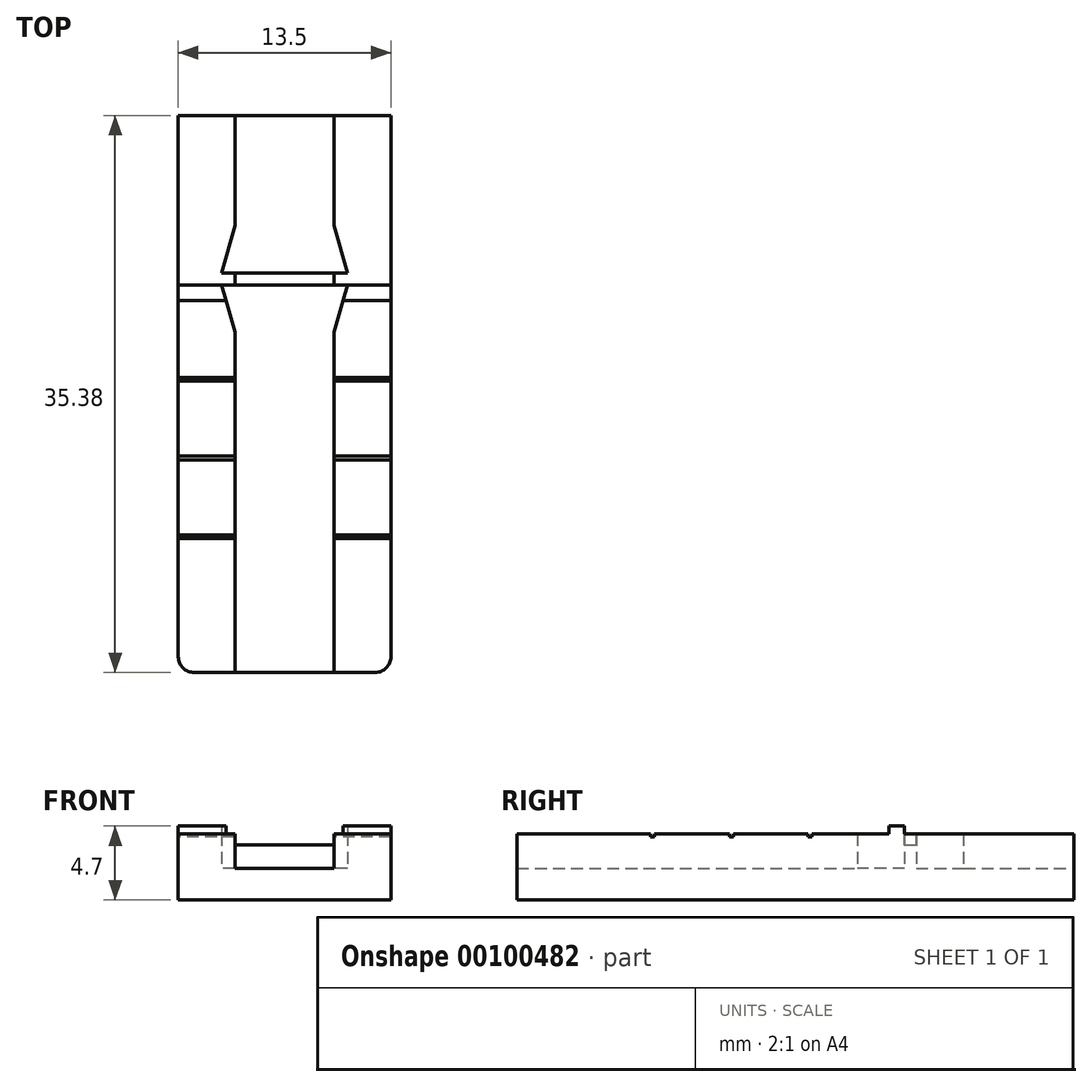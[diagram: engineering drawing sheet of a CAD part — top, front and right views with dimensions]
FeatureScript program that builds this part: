
annotation { "Feature Type Name" : "Feature", "Feature Type Description" : "" }
export const myFeature = defineFeature(function(context is Context, id is Id, definition is map)
    precondition{}
    {
        {
            var Q0;
            Q0=qCreatedBy(makeId("Front.planeOp"),FACE);
            var sketch = newSketch(context, id + "F0", { "sketchPlane" : qUnion([Q0])});
            skLineSegment(sketch, "E0", {"start": v(-6.75, 0) * mm, "end": v(6.75, 0) * mm});
            skLineSegment(sketch, "E1", {"start": v(6.75, 0) * mm, "end": v(6.75, 4.2) * mm});
            skLineSegment(sketch, "E2", {"start": v(6.75, 4.2) * mm, "end": v(3.15, 4.2) * mm});
            skLineSegment(sketch, "E3", {"start": v(3.15, 4.2) * mm, "end": v(3.15, 2) * mm});
            skLineSegment(sketch, "E4", {"start": v(3.15, 2) * mm, "end": v(-3.15, 2) * mm});
            skLineSegment(sketch, "E5", {"start": v(-3.15, 2) * mm, "end": v(-3.15, 4.2) * mm});
            skLineSegment(sketch, "E6", {"start": v(-3.15, 4.2) * mm, "end": v(-6.75, 4.2) * mm});
            skLineSegment(sketch, "E7", {"start": v(-6.75, 4.2) * mm, "end": v(-6.75, 0) * mm});
            skPoint(sketch, "E8", {"position": v(0, 2) * mm});
            skSolve(sketch);
        }
        {
            var Q0;
            Q0=qSketchRegion(id+"F0",true);
            extrude(context, id + "F1", {"entities" : qUnion([Q0]), "endBound" : BoundingType.SYMMETRIC, "depth" : 50 * mm});
        }
        {
            var Q0;
            Q0=makeQuery(id+"F1.opExtrude","SWEPT_FACE",FACE,{"disambiguationData":[OSD([sQuery(id+"F0.wireOp",EDGE,"E4")])]});
            var sketch = newSketch(context, id + "F2", { "sketchPlane" : qUnion([Q0])});
            skLineSegment(sketch, "E9.bottom", {"start": v(3.15, 0.38) * mm, "end": v(-3.15, 0.38) * mm});
            skLineSegment(sketch, "E9.top", {"start": v(3.15, -0.38) * mm, "end": v(-3.15, -0.38) * mm});
            skLineSegment(sketch, "E9.left", {"start": v(3.15, 0.38) * mm, "end": v(3.15, -0.38) * mm});
            skLineSegment(sketch, "E9.right", {"start": v(-3.15, 0.38) * mm, "end": v(-3.15, -0.38) * mm});
            skPoint(sketch, "E9.middle", {"position": v(0, 0) * mm});
            skSolve(sketch);
        }
        {
            var Q0;
            Q0=qSketchRegion(id+"F2",true);
            extrude(context, id + "F3", {"entities" : qUnion([Q0]), "operationType" : NewBodyOperationType.ADD, "depth" : 1.5 * mm});
        }
        {
            var Q0;
            Q0=makeQuery(id+"F1.opExtrude","SWEPT_FACE",FACE,{"disambiguationData":[OSD([sQuery(id+"F0.wireOp",EDGE,"E6")])]});
            var sketch = newSketch(context, id + "F4", { "sketchPlane" : qUnion([Q0])});
            skLineSegment(sketch, "E10.bottom", {"start": v(6.75, -0.37) * mm, "end": v(-6.75, -0.38) * mm});
            skLineSegment(sketch, "E10.top", {"start": v(6.75, -1.37) * mm, "end": v(-6.75, -1.38) * mm});
            skLineSegment(sketch, "E10.left", {"start": v(6.75, -0.38) * mm, "end": v(6.75, -1.37) * mm});
            skLineSegment(sketch, "E10.right", {"start": v(-6.75, -0.38) * mm, "end": v(-6.75, -1.38) * mm});
            skLineSegment(sketch, "E11", {"start": v(-3.15, -0.38) * mm, "end": v(-3.15, -1.38) * mm});
            skLineSegment(sketch, "E12", {"start": v(3.15, -1.38) * mm, "end": v(3.15, -0.38) * mm});
            skSolve(sketch);
        }
        {
            var Q0;
            {var subQ0=sQuery(id+"F4.wireOp",EDGE,"E10.left");Q0=makeQuery(id+"F4.imprint","IMPRINT",FACE,{"disambiguationData":[TD([[makeQuery(id+"F4.imprint","IMPRINT",EDGE,{"derivedFrom":subQ0}),-1.0]])]});}
            var Q1;
            {var subQ0=sQuery(id+"F4.wireOp",EDGE,"E10.right");Q1=makeQuery(id+"F4.imprint","IMPRINT",FACE,{"disambiguationData":[TD([[makeQuery(id+"F4.imprint","IMPRINT",EDGE,{"derivedFrom":subQ0}),-1.0]])]});}
            extrude(context, id + "F5", {"entities" : qUnion([Q0, Q1]), "operationType" : NewBodyOperationType.ADD, "depth" : .5 * mm});
        }
        {
            var Q0;
            {var subQ1=sQuery(id+"F4.wireOp",EDGE,"E10.right");var subQ2=sQuery(id+"F4.wireOp",EDGE,"E10.top");var subQ3=sQuery(id+"F0.wireOp",EDGE,"E7");var subQ4=sQuery(id+"F0.wireOp",EDGE,"E6");Q0=makeQuery(id+"F5.boolean.opBoolean","SPLIT",FACE,{"disambiguationData":[TD([makeQuery(id+"F5.opExtrude","SWEPT_FACE",FACE,{"disambiguationData":[OSD([subQ2]),TDD([makeQuery(id+"F4.imprint","IMPRINT",EDGE,{"disambiguationData":[TD([[makeQuery(id+"F4.imprint","INTERSECT",VERTEX,{"derivedFrom":[makeQuery(id+"F1.opExtrude","SWEPT_EDGE",EDGE,{"disambiguationData":[OSD([subQ4,subQ3])]}),subQ2,subQ1]}),1.0]])],"derivedFrom":subQ2})])]})])],"derivedFrom":makeQuery(id+"F1.opExtrude","SWEPT_FACE",FACE,{"disambiguationData":[OSD([subQ4])]})});}
            var sketch = newSketch(context, id + "F6", { "sketchPlane" : qUnion([Q0])});
            skLineSegment(sketch, "E13.bottom", {"start": v(6.75, -6.5) * mm, "end": v(-6.75, -6.5) * mm});
            skLineSegment(sketch, "E13.top", {"start": v(6.75, -6.25) * mm, "end": v(-6.75, -6.25) * mm});
            skLineSegment(sketch, "E13.left", {"start": v(6.75, -6.5) * mm, "end": v(6.75, -6.25) * mm});
            skLineSegment(sketch, "E13.right", {"start": v(-6.75, -6.5) * mm, "end": v(-6.75, -6.25) * mm});
            skPoint(sketch, "E13.middle", {"position": v(0, -6.37) * mm});
            skLineSegment(sketch, "E14.bottom", {"start": v(6.75, -11.5) * mm, "end": v(-6.75, -11.5) * mm});
            skLineSegment(sketch, "E14.top", {"start": v(6.75, -11.25) * mm, "end": v(-6.75, -11.25) * mm});
            skLineSegment(sketch, "E14.left", {"start": v(6.75, -11.5) * mm, "end": v(6.75, -11.25) * mm});
            skLineSegment(sketch, "E14.right", {"start": v(-6.75, -11.5) * mm, "end": v(-6.75, -11.25) * mm});
            skPoint(sketch, "E14.middle", {"position": v(0, -11.37) * mm});
            skLineSegment(sketch, "E15.bottom", {"start": v(6.75, -16.5) * mm, "end": v(-6.75, -16.5) * mm});
            skLineSegment(sketch, "E15.top", {"start": v(6.75, -16.25) * mm, "end": v(-6.75, -16.25) * mm});
            skLineSegment(sketch, "E15.left", {"start": v(6.75, -16.5) * mm, "end": v(6.75, -16.25) * mm});
            skLineSegment(sketch, "E15.right", {"start": v(-6.75, -16.5) * mm, "end": v(-6.75, -16.25) * mm});
            skPoint(sketch, "E15.middle", {"position": v(0, -16.37) * mm});
            skSolve(sketch);
        }
        {
            var Q0;
            Q0=qSketchRegion(id+"F6",true);
            extrude(context, id + "F7", {"entities" : qUnion([Q0]), "operationType" : NewBodyOperationType.REMOVE, "oppositeDirection" : true, "depth" : .2 * mm});
        }
        {
            var Q0;
            {var subQ0=sQuery(id+"F4.wireOp",EDGE,"E10.left");var subQ1=sQuery(id+"F4.wireOp",EDGE,"E10.bottom");var subQ5=sQuery(id+"F0.wireOp",EDGE,"E2");Q0=makeQuery(id+"F5.boolean.opBoolean","SPLIT",FACE,{"disambiguationData":[TD([makeQuery(id+"F5.opExtrude","SWEPT_FACE",FACE,{"disambiguationData":[OSD([subQ1]),TDD([makeQuery(id+"F4.imprint","IMPRINT",EDGE,{"disambiguationData":[TD([[makeQuery(id+"F4.imprint","INTERSECT",VERTEX,{"derivedFrom":[subQ1,subQ0]}),-1.0]])],"derivedFrom":subQ1})])]})])],"derivedFrom":makeQuery(id+"F1.opExtrude","SWEPT_FACE",FACE,{"disambiguationData":[OSD([subQ5])]})});}
            var sketch = newSketch(context, id + "F8", { "sketchPlane" : qUnion([Q0])});
            skLineSegment(sketch, "E16.bottom", {"start": v(6.75, 25) * mm, "end": v(-6.75, 25) * mm});
            skLineSegment(sketch, "E16.top", {"start": v(6.75, 10.38) * mm, "end": v(-6.75, 10.38) * mm});
            skLineSegment(sketch, "E16.left", {"start": v(6.75, 25) * mm, "end": v(6.75, 10.38) * mm});
            skLineSegment(sketch, "E16.right", {"start": v(-6.75, 25) * mm, "end": v(-6.75, 10.38) * mm});
            skSolve(sketch);
        }
        {
            var Q0;
            Q0=qSketchRegion(id+"F8",true);
            extrude(context, id + "F9", {"entities" : qUnion([Q0]), "operationType" : NewBodyOperationType.REMOVE, "endBound" : BoundingType.THROUGH_ALL, "oppositeDirection" : true, "depth" : 25 * mm});
        }
        {
            var Q0;
            Q0=makeQuery(id+"F9.boolean.opBoolean","COPY",EDGE,{"derivedFrom":makeQuery(id+"F9.opExtrude","SWEPT_EDGE",EDGE,{"disambiguationData":[OSD([sQuery(id+"F8.wireOp",EDGE,"E16.top"),sQuery(id+"F8.wireOp",EDGE,"E16.right")])]})});
            var Q1;
            Q1=makeQuery(id+"F9.boolean.opBoolean","COPY",EDGE,{"derivedFrom":makeQuery(id+"F9.opExtrude","SWEPT_EDGE",EDGE,{"disambiguationData":[OSD([sQuery(id+"F0.wireOp",EDGE,"E1"),sQuery(id+"F0.wireOp",EDGE,"E2"),sQuery(id+"F8.wireOp",EDGE,"E16.top"),sQuery(id+"F8.wireOp",EDGE,"E16.left")])]})});
            var Q2;
            Q2=makeQuery(id+"F1.opExtrude","CAP_EDGE",EDGE,{"disambiguationData":[OSD([sQuery(id+"F0.wireOp",EDGE,"E7")])],"isStart":false});
            var Q3;
            Q3=makeQuery(id+"F1.opExtrude","CAP_EDGE",EDGE,{"disambiguationData":[OSD([sQuery(id+"F0.wireOp",EDGE,"E1")])],"isStart":false});
            fillet(context, id + "F10", {"entities" : qUnion([Q0, Q1, Q2, Q3]), "radius" : 1 * mm, "tangentPropagation" : true, "allowEdgeOverflow" : false});
        }
        {
            var Q0;
            {var subQ1=sQuery(id+"F0.wireOp",EDGE,"E4");Q0=makeQuery(id+"F3.boolean.opBoolean","SPLIT",FACE,{"disambiguationData":[TD([makeQuery(id+"F3.opExtrude","SWEPT_FACE",FACE,{"disambiguationData":[OSD([sQuery(id+"F2.wireOp",EDGE,"E9.top")])]})])],"derivedFrom":makeQuery(id+"F1.opExtrude","SWEPT_FACE",FACE,{"disambiguationData":[OSD([subQ1])]})});}
            var sketch = newSketch(context, id + "F11", { "sketchPlane" : qUnion([Q0])});
            skLineSegment(sketch, "E17", {"start": v(-4, -0.38) * mm, "end": v(4, -0.38) * mm});
            skLineSegment(sketch, "E18", {"start": v(4, -0.37) * mm, "end": v(3.15, -3.38) * mm});
            skLineSegment(sketch, "E19", {"start": v(-3.15, -3.38) * mm, "end": v(-4, -0.37) * mm});
            skLineSegment(sketch, "E20", {"start": v(3.15, -3.38) * mm, "end": v(-3.15, -3.38) * mm});
            skLineSegment(sketch, "E21", {"start": v(-3.15, 0) * mm, "end": v(3.15, 0) * mm, "construction": true});
            skLineSegment(sketch, "E22.MirrorCS", {"start": v(-4, 0.38) * mm, "end": v(4, 0.38) * mm});
            skLineSegment(sketch, "E23.MirrorCS", {"start": v(3.15, 3.38) * mm, "end": v(-3.15, 3.38) * mm});
            skLineSegment(sketch, "E24.MirrorCS", {"start": v(-3.15, 3.38) * mm, "end": v(-4, 0.37) * mm});
            skLineSegment(sketch, "E25.MirrorCS", {"start": v(4, 0.37) * mm, "end": v(3.15, 3.38) * mm});
            skSolve(sketch);
        }
        {
            var Q0;
            Q0=qSketchRegion(id+"F11",true);
            extrude(context, id + "F12", {"entities" : qUnion([Q0]), "operationType" : NewBodyOperationType.REMOVE, "endBound" : BoundingType.THROUGH_ALL, "depth" : 25 * mm});
        }
    });
